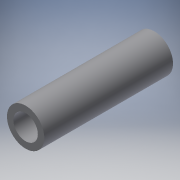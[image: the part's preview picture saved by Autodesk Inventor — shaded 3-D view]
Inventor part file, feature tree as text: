
AUTODESK INVENTOR PART (.ipt)
format: ipt  version: 2018 (Build 220112000, 112)  size: 97,792 bytes
history: native  units: mm
features: extrude x1, sketch x1
ambient origin geometry x8: Origin, YZ Plane, XZ Plane, XY Plane, X Axis, Y Axis, Z Axis, Center Point
bodies: Volumenkörper1 (feature_tree)
feature tree (2):
  extrude  "Extrusion1"  Depth=20.0mm
  sketch  "Skizze1"  dims[d0=3.8mm d1=1.0mm d2=20.0mm d3=0.0mm]
